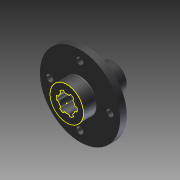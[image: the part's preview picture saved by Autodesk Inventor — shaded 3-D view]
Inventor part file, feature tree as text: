
AUTODESK INVENTOR PART (.ipt)
format: ipt  version: 2014 SP1 (Build 180222100, 222)  size: 178,176 bytes
history: native  units: in
note: dims shown in document units (in); Inventor stores cm internally (conversion verified against a paired STEP export)
features: other x1, sketch x1, imported_body x1
ambient origin geometry x8: Origin, YZ Plane, XZ Plane, XY Plane, X Axis, Y Axis, Z Axis, Center Point
bodies: Solid1 (feature_tree)
feature tree (3):
  other  "nippondensogearcoupler2.ipt1"
  sketch  "Sketch1"
  imported_body  "Base1"
